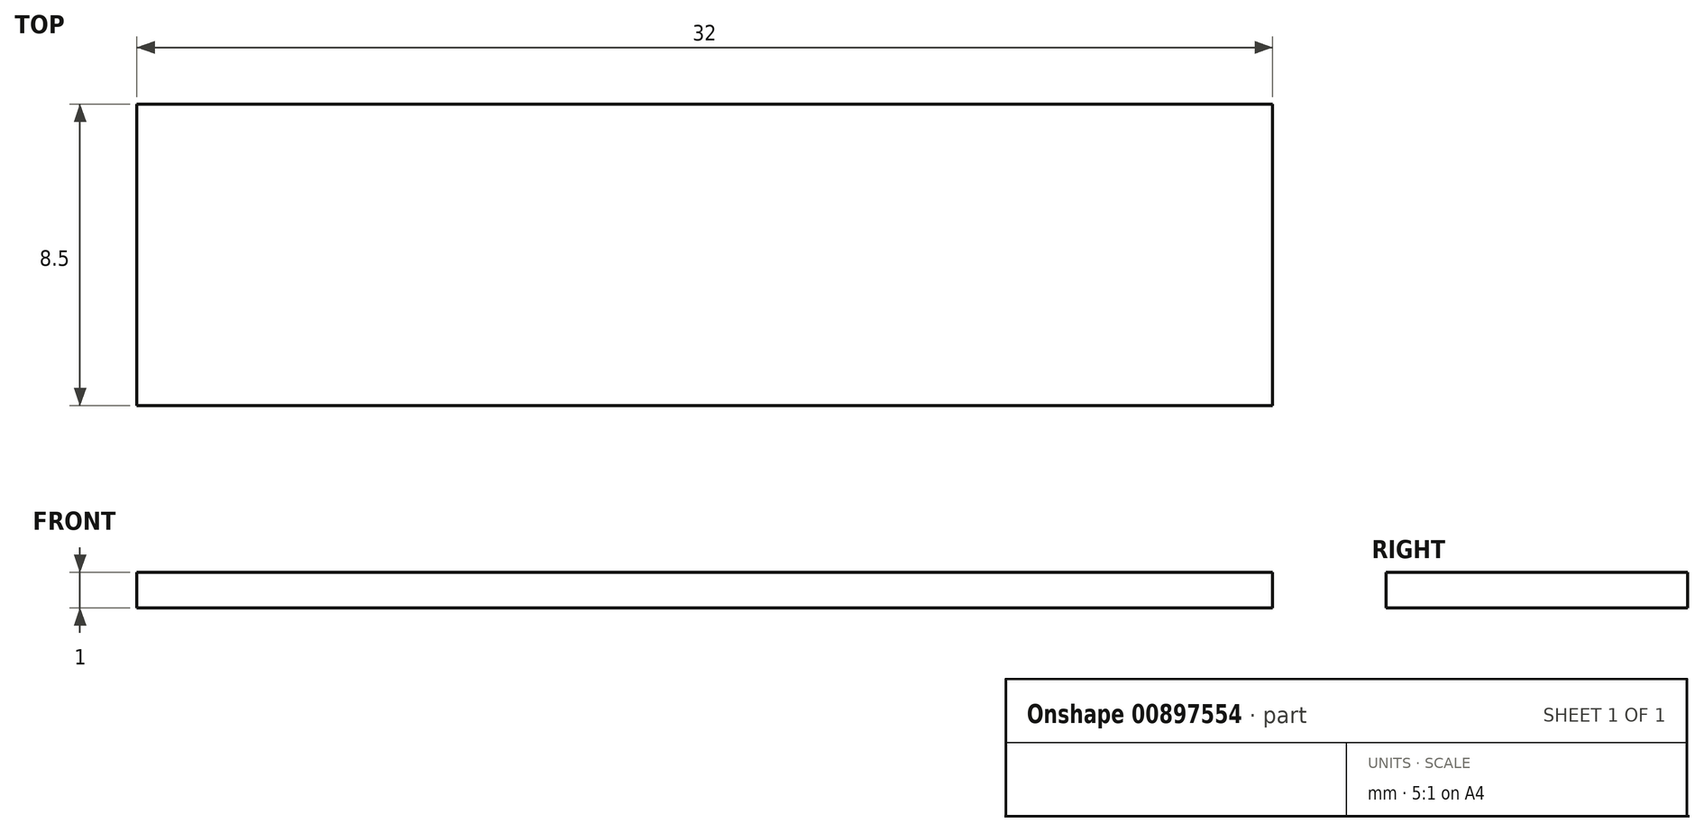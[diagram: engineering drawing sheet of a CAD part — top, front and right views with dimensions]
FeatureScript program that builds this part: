
annotation { "Feature Type Name" : "Feature", "Feature Type Description" : "" }
export const myFeature = defineFeature(function(context is Context, id is Id, definition is map)
    precondition{}
    {
        {
            var Q0;
            Q0=qCreatedBy(makeId("Top.planeOp"),FACE);
            var sketch = newSketch(context, id + "F0", { "sketchPlane" : qUnion([Q0])});
            skLineSegment(sketch, "E0.bottom", {"start": v(-54.23, 32.46) * mm, "end": v(-22.23, 32.46) * mm});
            skLineSegment(sketch, "E0.top", {"start": v(-54.23, 23.96) * mm, "end": v(-22.23, 23.96) * mm});
            skLineSegment(sketch, "E0.left", {"start": v(-54.23, 32.46) * mm, "end": v(-54.23, 23.96) * mm});
            skLineSegment(sketch, "E0.right", {"start": v(-22.23, 32.46) * mm, "end": v(-22.23, 23.96) * mm});
            skSolve(sketch);
        }
        {
            var Q0;
            Q0 = qSketchRegion(id + "F0", true);
            extrude(context, id + "F1", {"entities" : qUnion([Q0]), "depth" : 1 * mm, "offsetDistance" : 25 * mm});
        }
    });
